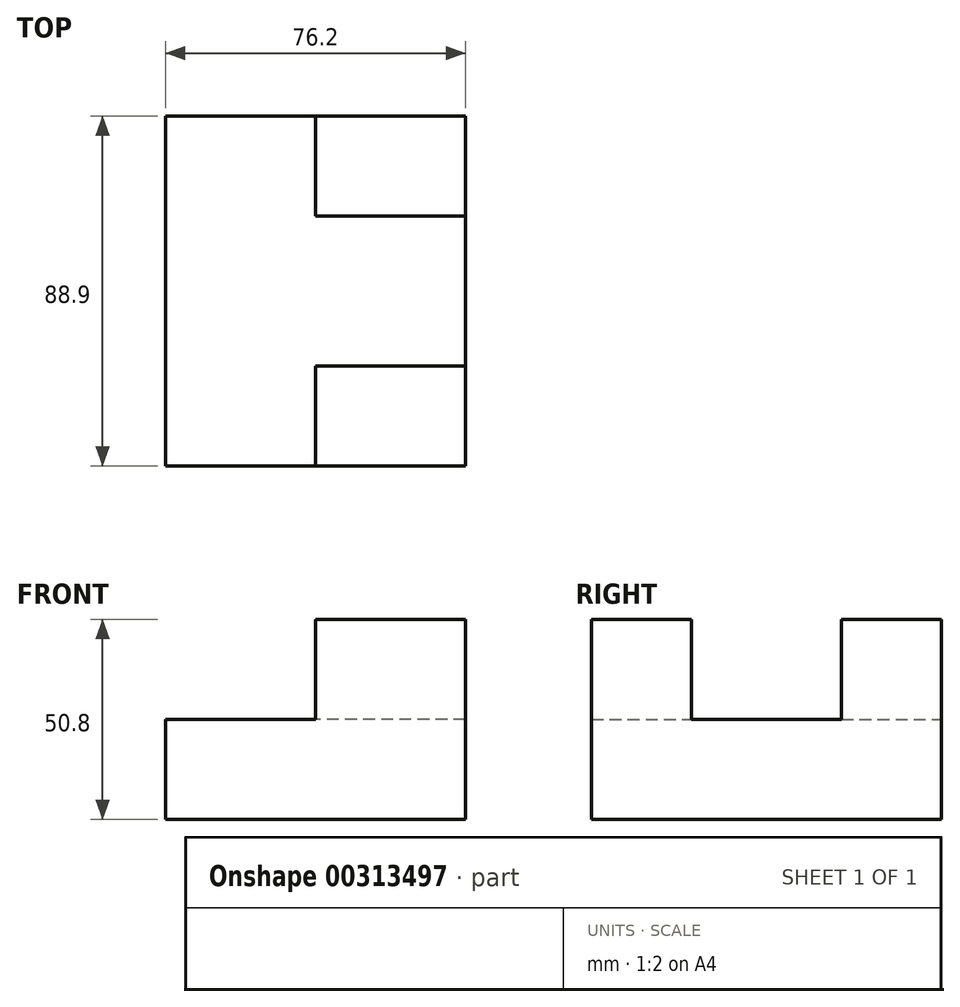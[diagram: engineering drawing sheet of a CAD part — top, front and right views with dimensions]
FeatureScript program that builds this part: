
annotation { "Feature Type Name" : "Feature", "Feature Type Description" : "" }
export const myFeature = defineFeature(function(context is Context, id is Id, definition is map)
    precondition{}
    {
        {
            var Q0;
            Q0=qCreatedBy(makeId("Front.planeOp"),FACE);
            var sketch = newSketch(context, id + "F0", { "sketchPlane" : qUnion([Q0])});
            skLineSegment(sketch, "E0", {"start": v(-46.13, -48.68) * mm, "end": v(30.07, -48.68) * mm});
            skLineSegment(sketch, "E1", {"start": v(30.07, 14.82) * mm, "end": v(-8.03, 14.82) * mm});
            skLineSegment(sketch, "E2", {"start": v(-8.03, 14.82) * mm, "end": v(-8.03, -10.58) * mm});
            skLineSegment(sketch, "E3", {"start": v(30.07, 14.82) * mm, "end": v(30.07, -48.68) * mm});
            skLineSegment(sketch, "E4", {"start": v(-8.03, -10.58) * mm, "end": v(-46.13, -10.58) * mm});
            skLineSegment(sketch, "E5", {"start": v(-46.13, -10.58) * mm, "end": v(-46.13, -48.68) * mm});
            skSolve(sketch);
        }
        {
            var Q0;
            Q0=makeQuery(id+"F0.imprint","IMPRINT",FACE,{"disambiguationData":[TD([[makeQuery(id+"F0.imprint","IMPRINT",EDGE,{"derivedFrom":sQuery(id+"F0.wireOp",EDGE,"E0")}),1.0]])]});
            extrude(context, id + "F1", {"entities" : qUnion([Q0]), "depth" : 88.9 * mm});
        }
        {
            var Q0;
            Q0=makeQuery(id+"F1.opExtrude","SWEPT_FACE",FACE,{"disambiguationData":[OSD([sQuery(id+"F0.wireOp",EDGE,"E1")])]});
            var sketch = newSketch(context, id + "F2", { "sketchPlane" : qUnion([Q0])});
            skLineSegment(sketch, "E6", {"start": v(30.07, -88.9) * mm, "end": v(30.07, -63.5) * mm});
            skLineSegment(sketch, "E7", {"start": v(30.07, -63.5) * mm, "end": v(-8.03, -63.5) * mm});
            skLineSegment(sketch, "E8", {"start": v(30.07, 0) * mm, "end": v(30.07, -25.4) * mm});
            skLineSegment(sketch, "E9", {"start": v(30.07, -25.4) * mm, "end": v(-8.03, -25.4) * mm});
            skSolve(sketch);
        }
        {
            var Q0;
            Q0=makeQuery(id+"F2.imprint","IMPRINT",FACE,{"disambiguationData":[TD([[makeQuery(id+"F2.imprint","IMPRINT",EDGE,{"derivedFrom":sQuery(id+"F2.wireOp",EDGE,"E6")}),1.0]])]});
            extrude(context, id + "F3", {"entities" : qUnion([Q0]), "operationType" : NewBodyOperationType.REMOVE, "oppositeDirection" : true, "depth" : 12.7 * mm});
        }
        {
            var Q0;
            Q0=makeQuery(id+"F1.opExtrude","SWEPT_FACE",FACE,{"disambiguationData":[OSD([sQuery(id+"F0.wireOp",EDGE,"E1")])]});
            extrude(context, id + "F4", {"entities" : qUnion([Q0]), "operationType" : NewBodyOperationType.REMOVE, "oppositeDirection" : true, "depth" : 12.7 * mm});
        }
        {
            var Q0;
            Q0=makeQuery(id+"F1.opExtrude","SWEPT_FACE",FACE,{"disambiguationData":[OSD([sQuery(id+"F0.wireOp",EDGE,"E4")])]});
            extrude(context, id + "F5", {"entities" : qUnion([Q0]), "operationType" : NewBodyOperationType.REMOVE, "oppositeDirection" : true, "depth" : 12.7 * mm});
        }
        {
            var Q0;
            {var subQ0=sQuery(id+"F0.wireOp",EDGE,"E1");Q0=makeQuery(id+"F4.boolean.opBoolean","MERGE",FACE,{"derivedFrom":[makeQuery(id+"F3.boolean.opBoolean","COPY",FACE,{"derivedFrom":makeQuery(id+"F3.opExtrude","CAP_FACE",FACE,{"disambiguationData":[OSD([subQ0,sQuery(id+"F0.wireOp",EDGE,"E2"),sQuery(id+"F2.wireOp",EDGE,"E6"),sQuery(id+"F2.wireOp",EDGE,"E7")])],"isStart":false})}),makeQuery(id+"F4.opExtrude","CAP_FACE",FACE,{"disambiguationData":[OSD([subQ0])],"isStart":false})]});}
            var sketch = newSketch(context, id + "F6", { "sketchPlane" : qUnion([Q0])});
            skLineSegment(sketch, "E10", {"start": v(30.07, 0) * mm, "end": v(30.07, -25.4) * mm});
            skLineSegment(sketch, "E11", {"start": v(30.07, -88.9) * mm, "end": v(30.07, -63.5) * mm});
            skLineSegment(sketch, "E12", {"start": v(30.07, -63.5) * mm, "end": v(-8.03, -63.5) * mm});
            skLineSegment(sketch, "E13", {"start": v(30.07, -25.4) * mm, "end": v(-8.03, -25.4) * mm});
            skSolve(sketch);
        }
        {
            var Q0;
            {var subQ0=sQuery(id+"F6.wireOp",EDGE,"E12");Q0=makeQuery(id+"F6.imprint","IMPRINT",FACE,{"disambiguationData":[TD([[makeQuery(id+"F6.imprint","IMPRINT",EDGE,{"derivedFrom":subQ0}),-1.0]])]});}
            extrude(context, id + "F7", {"entities" : qUnion([Q0]), "operationType" : NewBodyOperationType.REMOVE, "oppositeDirection" : true, "depth" : 25.4 * mm});
        }
    });
